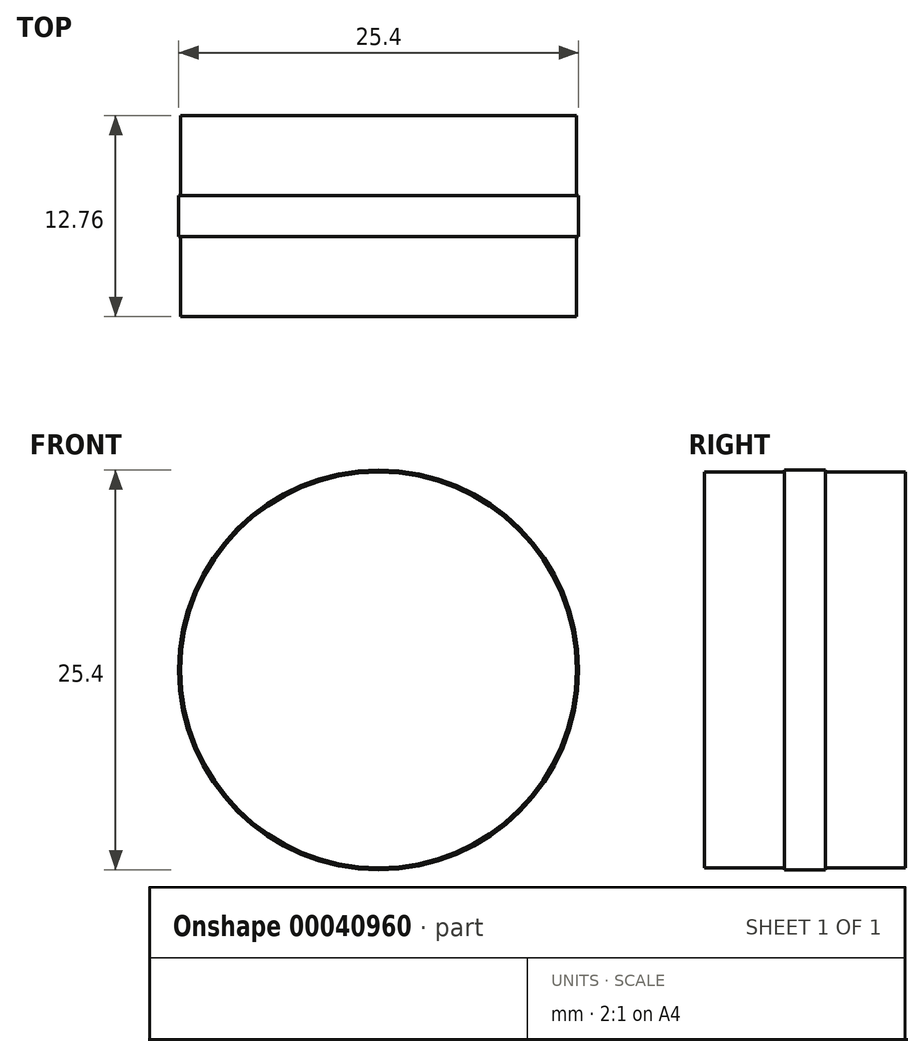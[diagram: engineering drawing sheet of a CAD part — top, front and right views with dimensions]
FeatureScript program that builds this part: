
annotation { "Feature Type Name" : "Feature", "Feature Type Description" : "" }
export const myFeature = defineFeature(function(context is Context, id is Id, definition is map)
    precondition{}
    {
        {
            var Q0;
            Q0=qCreatedBy(makeId("Front.planeOp"),FACE);
            var sketch = newSketch(context, id + "F0", { "sketchPlane" : qUnion([Q0])});
            skCircle(sketch, "E0", {"center": v(0, 0) * mm, "radius": 12.7 * mm});
            skSolve(sketch);
        }
        {
            var Q0;
            Q0=makeQuery(id+"F0.imprint","IMPRINT",FACE,{"disambiguationData":[TD([[makeQuery(id+"F0.imprint","IMPRINT",EDGE,{"derivedFrom":sQuery(id+"F0.wireOp",EDGE,"E0")}),1.0]])]});
            extrude(context, id + "F1", {"entities" : qUnion([Q0]), "depth" : 1.3 * mm, "hasSecondDirection" : true, "secondDirectionOppositeDirection" : true, "secondDirectionDepth" : 1.3 * mm});
        }
        {
            var Q0;
            Q0=makeQuery(id+"F1.opExtrude","CAP_FACE",FACE,{"disambiguationData":[OSD([sQuery(id+"F0.wireOp",EDGE,"E0")])],"isStart":false});
            var sketch = newSketch(context, id + "F2", { "sketchPlane" : qUnion([Q0])});
            skCircle(sketch, "E1", {"center": v(0, 0) * mm, "radius": 12.57 * mm});
            skSolve(sketch);
        }
        {
            var Q0;
            Q0=makeQuery(id+"F2.imprint","IMPRINT",FACE,{"disambiguationData":[TD([[makeQuery(id+"F2.imprint","IMPRINT",EDGE,{"derivedFrom":sQuery(id+"F2.wireOp",EDGE,"E1")}),1.0]])]});
            extrude(context, id + "F3", {"entities" : qUnion([Q0]), "operationType" : NewBodyOperationType.ADD, "depth" : 5.08 * mm});
        }
        {
            var Q0;
            Q0=makeQuery(id+"F1.opExtrude","CAP_FACE",FACE,{"disambiguationData":[OSD([sQuery(id+"F0.wireOp",EDGE,"E0")])],"isStart":true});
            var sketch = newSketch(context, id + "F4", { "sketchPlane" : qUnion([Q0])});
            skCircle(sketch, "E2", {"center": v(0, 0) * mm, "radius": 12.57 * mm});
            skSolve(sketch);
        }
        {
            var Q0;
            Q0=makeQuery(id+"F4.imprint","IMPRINT",FACE,{"disambiguationData":[TD([[makeQuery(id+"F4.imprint","IMPRINT",EDGE,{"derivedFrom":sQuery(id+"F4.wireOp",EDGE,"E2")}),1.0]])]});
            extrude(context, id + "F5", {"entities" : qUnion([Q0]), "operationType" : NewBodyOperationType.ADD, "depth" : 5.08 * mm});
        }
    });
